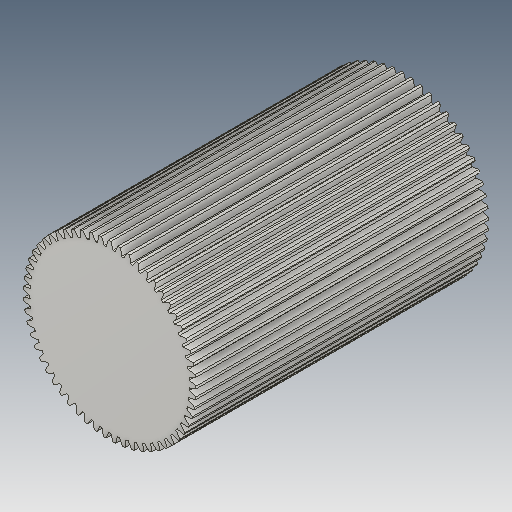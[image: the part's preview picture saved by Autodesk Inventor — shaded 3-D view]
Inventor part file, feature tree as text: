
AUTODESK INVENTOR PART (.ipt)
format: ipt  version: 2021 (Build 250183000, 183)  size: 463,360 bytes
history: native  units: mm (DEFAULTED — no unit token found)
features: plane x3, other x3, sketch x2, extrude x1
ambient origin geometry x8: Origin, YZ Plane, XZ Plane, XY Plane, X Axis, Y Axis, Z Axis, Center Point
bodies: Solid1 (feature_tree)
feature tree (9):
  extrude  "Extrusion1"  Depth=20.0mm TaperAngle=0.0deg
  plane  "Work Plane2"
  plane  "Work Plane8"
  plane  "Work Plane9"
  other  "Engrenagem reta"
  sketch  "Sketch1"  dims[d0=11.8mm d1=20.0mm d2=0.0mm]
  sketch  "Sketch2"  dims[d3=11.4mm d4=10.0mm d5=0.0mm d16=10.7mm d17=0.0mm d34=0.551157mm d39=0.0mm d41=0.0mm d43=10.7mm d46=10.7mm d47=0.0mm d48=0.0mm]
  other  "Srf1"
  other  "Diâmetro do flanco"
